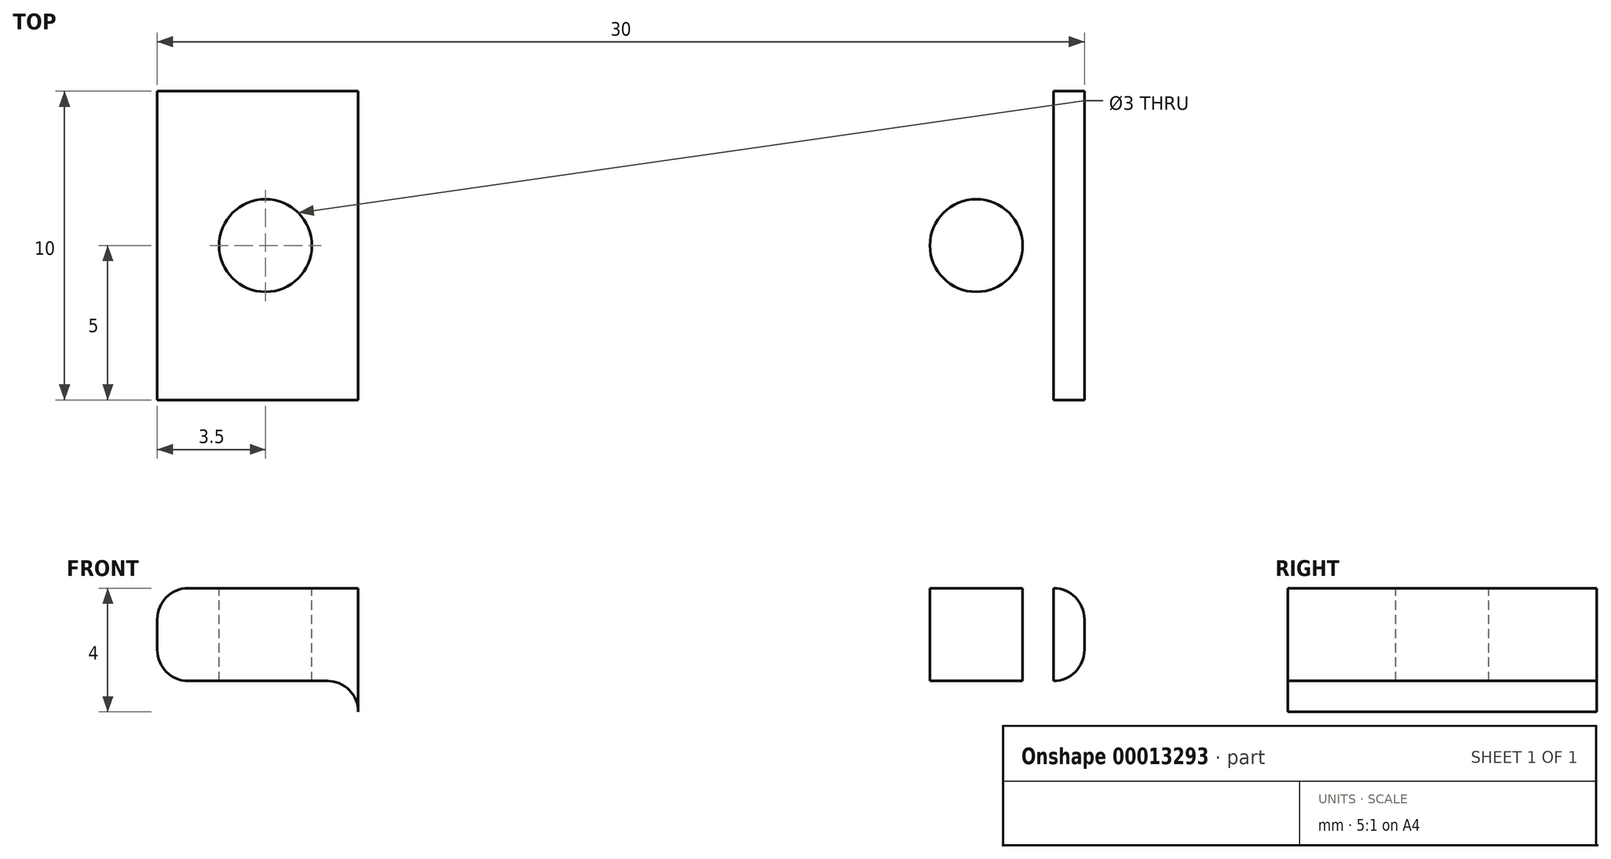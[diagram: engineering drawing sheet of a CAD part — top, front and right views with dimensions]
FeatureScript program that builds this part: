
annotation { "Feature Type Name" : "Feature", "Feature Type Description" : "" }
export const myFeature = defineFeature(function(context is Context, id is Id, definition is map)
    precondition{}
    {
        {
            var Q0;
            Q0=qCreatedBy(makeId("Front.planeOp"),FACE);
            var sketch = newSketch(context, id + "F0", { "sketchPlane" : qUnion([Q0])});
            skLineSegment(sketch, "E0", {"start": v(0, -10.68) * mm, "end": v(0, 14.02) * mm, "construction": true});
            skLineSegment(sketch, "E1", {"start": v(0, 8.5) * mm, "end": v(-14, 8.5) * mm});
            skLineSegment(sketch, "E2", {"start": v(-15, 7.5) * mm, "end": v(-15, 6.5) * mm});
            skLineSegment(sketch, "E3", {"start": v(-14, 5.5) * mm, "end": v(-9.5, 5.5) * mm});
            skCircle(sketch, "E4", {"center": v(0, 0) * mm, "radius": 8.5 * mm});
            skLineSegment(sketch, "E5", {"start": v(-8.5, 0) * mm, "end": v(-8.5, 4.5) * mm});
            skCircle(sketch, "E6", {"center": v(0, 0) * mm, "radius": 6.5 * mm});
            skPoint(sketch, "E7", {"position": v(4, 0) * mm});
            skPoint(sketch, "E8", {"position": v(3.46, 2) * mm});
            skLineSegment(sketch, "E9", {"start": v(0, 0) * mm, "end": v(3.46, 2) * mm, "construction": true});
            skArc(sketch, "E10", {"start": v(3.46, 2) * mm, "mid": v(-3.86, -1.03) * mm, "end": v(4, 0) * mm, "construction": true});
            skArc(sketch, "E11", {"start": v(4, 0) * mm, "mid": v(3.86, 1.03) * mm, "end": v(3.46, 2) * mm});
            skArc(sketch, "E12.0", {"start": v(5, -0.01) * mm, "mid": v(4.83, 1.29) * mm, "end": v(4.33, 2.5) * mm});
            skLineSegment(sketch, "E13", {"start": v(3.46, 2) * mm, "end": v(4.33, 2.5) * mm, "construction": true});
            skPoint(sketch, "E14", {"position": v(3.9, 2.25) * mm});
            skArc(sketch, "E15", {"start": v(4.33, 2.5) * mm, "mid": v(3.65, 2.68) * mm, "end": v(3.46, 2) * mm});
            skArc(sketch, "E16", {"start": v(5, -0.01) * mm, "mid": v(5.6, -0.67) * mm, "end": v(6.48, -0.47) * mm});
            skLineSegment(sketch, "E17", {"start": v(4, 0) * mm, "end": v(5.48, -3.5) * mm});
            skArc(sketch, "E18.1.0", {"start": v(1.55, 4.75) * mm, "mid": v(2.37, 5.13) * mm, "end": v(2.45, 6.02) * mm});
            skArc(sketch, "E18.1.1", {"start": v(1.55, 4.75) * mm, "mid": v(0.27, 5) * mm, "end": v(-1.04, 4.9) * mm});
            skArc(sketch, "E18.1.2", {"start": v(-1.04, 4.9) * mm, "mid": v(-1.42, 4.3) * mm, "end": v(-0.83, 3.91) * mm});
            skArc(sketch, "E18.1.3", {"start": v(1.24, 3.8) * mm, "mid": v(0.21, 4) * mm, "end": v(-0.83, 3.91) * mm});
            skLineSegment(sketch, "E18.1.4", {"start": v(1.24, 3.8) * mm, "end": v(5.02, 4.13) * mm});
            skArc(sketch, "E18.2.0", {"start": v(-4.04, 2.95) * mm, "mid": v(-4.15, 3.84) * mm, "end": v(-4.97, 4.2) * mm});
            skArc(sketch, "E18.2.1", {"start": v(-4.04, 2.95) * mm, "mid": v(-4.67, 1.8) * mm, "end": v(-4.97, 0.52) * mm});
            skArc(sketch, "E18.2.2", {"start": v(-4.97, 0.52) * mm, "mid": v(-4.53, -0.03) * mm, "end": v(-3.98, 0.42) * mm});
            skArc(sketch, "E18.2.3", {"start": v(-3.23, 2.36) * mm, "mid": v(-3.73, 1.44) * mm, "end": v(-3.98, 0.42) * mm});
            skLineSegment(sketch, "E18.2.4", {"start": v(-3.24, 2.35) * mm, "end": v(-2.38, 6.05) * mm});
            skArc(sketch, "E18.3.0", {"start": v(-4.05, -2.93) * mm, "mid": v(-4.93, -2.76) * mm, "end": v(-5.52, -3.43) * mm});
            skArc(sketch, "E18.3.1", {"start": v(-4.05, -2.93) * mm, "mid": v(-3.15, -3.88) * mm, "end": v(-2.03, -4.57) * mm});
            skArc(sketch, "E18.3.2", {"start": v(-2.03, -4.57) * mm, "mid": v(-1.37, -4.31) * mm, "end": v(-1.63, -3.65) * mm});
            skArc(sketch, "E18.3.3", {"start": v(-3.24, -2.34) * mm, "mid": v(-2.52, -3.1) * mm, "end": v(-1.63, -3.65) * mm});
            skLineSegment(sketch, "E18.3.4", {"start": v(-3.24, -2.35) * mm, "end": v(-6.49, -0.4) * mm});
            skArc(sketch, "E18.4.0", {"start": v(1.54, -4.76) * mm, "mid": v(1.1, -5.54) * mm, "end": v(1.55, -6.31) * mm});
            skArc(sketch, "E18.4.1", {"start": v(1.54, -4.76) * mm, "mid": v(2.72, -4.2) * mm, "end": v(3.72, -3.35) * mm});
            skArc(sketch, "E18.4.2", {"start": v(3.72, -3.35) * mm, "mid": v(3.68, -2.64) * mm, "end": v(2.97, -2.68) * mm});
            skArc(sketch, "E18.4.3", {"start": v(1.23, -3.8) * mm, "mid": v(2.18, -3.36) * mm, "end": v(2.97, -2.68) * mm});
            skLineSegment(sketch, "E18.4.4", {"start": v(1.24, -3.8) * mm, "end": v(-1.63, -6.3) * mm});
            skPoint(sketch, "E19.visualSharp", {"position": v(-15, 5.5) * mm});
            skArc(sketch, "E19.filletArc", {"start": v(-15, 6.5) * mm, "mid": v(-14.7, 5.8) * mm, "end": v(-14, 5.5) * mm});
            skPoint(sketch, "E20.visualSharp", {"position": v(-8.5, 5.5) * mm});
            skArc(sketch, "E20.filletArc", {"start": v(-8.5, 4.5) * mm, "mid": v(-8.8, 5.2) * mm, "end": v(-9.5, 5.5) * mm});
            skPoint(sketch, "E21.visualSharp", {"position": v(-15, 8.5) * mm});
            skArc(sketch, "E21.filletArc", {"start": v(-14, 8.5) * mm, "mid": v(-14.7, 8.2) * mm, "end": v(-15, 7.5) * mm});
            skLineSegment(sketch, "E22.0.MirrorCS", {"start": v(0, 8.5) * mm, "end": v(14, 8.5) * mm});
            skArc(sketch, "E23.0.MirrorCS", {"start": v(14, 8.5) * mm, "mid": v(14.7, 8.2) * mm, "end": v(15, 7.5) * mm});
            skLineSegment(sketch, "E24.0.MirrorCS", {"start": v(15, 7.5) * mm, "end": v(15, 6.5) * mm});
            skArc(sketch, "E25.0.MirrorCS", {"start": v(15, 6.5) * mm, "mid": v(14.7, 5.8) * mm, "end": v(14, 5.5) * mm});
            skLineSegment(sketch, "E26.0.MirrorCS", {"start": v(14, 5.5) * mm, "end": v(9.5, 5.5) * mm});
            skArc(sketch, "E27.0.MirrorCS", {"start": v(8.5, 4.5) * mm, "mid": v(8.8, 5.2) * mm, "end": v(9.5, 5.5) * mm});
            skLineSegment(sketch, "E28.0.MirrorCS", {"start": v(8.5, 0) * mm, "end": v(8.5, 4.5) * mm});
            skSolve(sketch);
        }
        {
            var Q0;
            {var subQ2=sQuery(id+"F0.wireOp",EDGE,"E1");Q0=makeQuery(id+"F0.imprint","IMPRINT",FACE,{"disambiguationData":[TD([[makeQuery(id+"F0.imprint","IMPRINT",EDGE,{"derivedFrom":subQ2}),1.0]])]});}
            var Q1;
            {var subQ1=sQuery(id+"F0.wireOp",EDGE,"E22.0.MirrorCS");Q1=makeQuery(id+"F0.imprint","IMPRINT",FACE,{"disambiguationData":[TD([[makeQuery(id+"F0.imprint","IMPRINT",EDGE,{"derivedFrom":subQ1}),-1.0]])]});}
            var Q2;
            {var subQ11=sQuery(id+"F0.wireOp",EDGE,"E4");var subQ13=makeQuery(id+"F0.imprint","INTERSECT",VERTEX,{"derivedFrom":[subQ11,sQuery(id+"F0.wireOp",EDGE,"E5")]});Q2=makeQuery(id+"F0.imprint","IMPRINT",FACE,{"disambiguationData":[TD([[makeQuery(id+"F0.imprint","IMPRINT",EDGE,{"disambiguationData":[TD([[subQ13,-1.0]])],"derivedFrom":subQ11}),1.0]])]});}
            var Q3;
            {var subQ3=sQuery(id+"F0.wireOp",EDGE,"E18.1.0");Q3=makeQuery(id+"F0.imprint","IMPRINT",FACE,{"disambiguationData":[TD([[makeQuery(id+"F0.imprint","IMPRINT",EDGE,{"derivedFrom":subQ3}),-1.0]])]});}
            var Q4;
            {var subQ3=sQuery(id+"F0.wireOp",EDGE,"E18.2.0");Q4=makeQuery(id+"F0.imprint","IMPRINT",FACE,{"disambiguationData":[TD([[makeQuery(id+"F0.imprint","IMPRINT",EDGE,{"derivedFrom":subQ3}),-1.0]])]});}
            var Q5;
            {var subQ3=sQuery(id+"F0.wireOp",EDGE,"E18.3.0");Q5=makeQuery(id+"F0.imprint","IMPRINT",FACE,{"disambiguationData":[TD([[makeQuery(id+"F0.imprint","IMPRINT",EDGE,{"derivedFrom":subQ3}),-1.0]])]});}
            var Q6;
            Q6=makeQuery(id+"F0.imprint","IMPRINT",FACE,{"disambiguationData":[TD([[makeQuery(id+"F0.imprint","IMPRINT",EDGE,{"derivedFrom":sQuery(id+"F0.wireOp",EDGE,"E12.0")}),1.0]])]});
            var Q7;
            {var subQ3=sQuery(id+"F0.wireOp",EDGE,"E18.4.0");Q7=makeQuery(id+"F0.imprint","IMPRINT",FACE,{"disambiguationData":[TD([[makeQuery(id+"F0.imprint","IMPRINT",EDGE,{"derivedFrom":subQ3}),-1.0]])]});}
            extrude(context, id + "F1", {"entities" : qUnion([Q0, Q1, Q2, Q3, Q4, Q5, Q6, Q7]), "depth" : 10 * mm});
        }
        {
            var Q0;
            Q0=makeQuery(id+"F1.opExtrude","SWEPT_FACE",FACE,{"disambiguationData":[OSD([sQuery(id+"F0.wireOp",EDGE,"E1"),sQuery(id+"F0.wireOp",EDGE,"E22.0.MirrorCS")])]});
            var sketch = newSketch(context, id + "F2", { "sketchPlane" : qUnion([Q0])});
            skLineSegment(sketch, "E29", {"start": v(-14, -5) * mm, "end": v(14, -5) * mm, "construction": true});
            skLineSegment(sketch, "E30", {"start": v(0, 0) * mm, "end": v(0, -10) * mm, "construction": true});
            skCircle(sketch, "E31", {"center": v(-11.5, -5) * mm, "radius": 1.5 * mm});
            skCircle(sketch, "E32.0.MirrorC", {"center": v(11.5, -5) * mm, "radius": 1.5 * mm});
            skLineSegment(sketch, "E33.0.1", {"start": v(-8.5, 0) * mm, "end": v(-8.5, -10) * mm});
            skLineSegment(sketch, "E33.0.3", {"start": v(-8.5, -10) * mm, "end": v(-8.5, 0) * mm});
            skSolve(sketch);
        }
        {
            var Q0;
            Q0=makeQuery(id+"F2.imprint","IMPRINT",FACE,{"disambiguationData":[TD([[makeQuery(id+"F2.imprint","IMPRINT",EDGE,{"derivedFrom":sQuery(id+"F2.wireOp",EDGE,"E31")}),1.0]])]});
            var Q1;
            Q1=makeQuery(id+"F2.imprint","IMPRINT",FACE,{"disambiguationData":[TD([[makeQuery(id+"F2.imprint","IMPRINT",EDGE,{"derivedFrom":sQuery(id+"F2.wireOp",EDGE,"E32.0.MirrorC")}),-1.0]])]});
            extrude(context, id + "F3", {"entities" : qUnion([Q0, Q1]), "operationType" : NewBodyOperationType.REMOVE, "endBound" : BoundingType.THROUGH_ALL, "oppositeDirection" : true, "depth" : 25 * mm});
        }
    });
